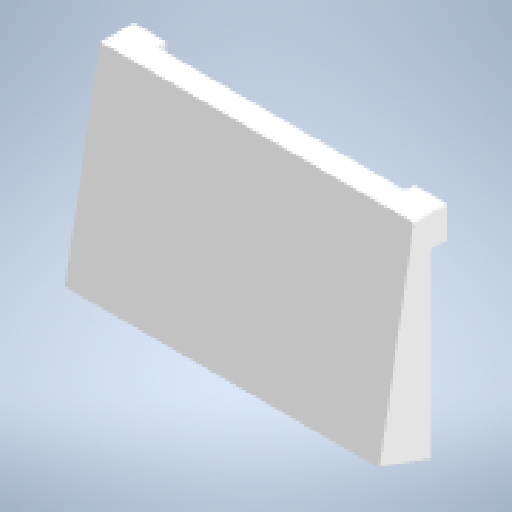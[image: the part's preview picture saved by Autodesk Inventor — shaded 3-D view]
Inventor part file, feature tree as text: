
AUTODESK INVENTOR PART (.ipt)
format: ipt  version: 2024 (Build 280153000, 153)  size: 190,464 bytes
history: native  units: mm
features: extrude x3, sketch x3, projected_geometry x3, fillet x2, plane x1
ambient origin geometry x8: Origin, YZ Plane, XZ Plane, XY Plane, X Axis, Y Axis, Z Axis, Center Point
bodies: Solid1 (feature_tree)
feature tree (12):
  extrude  "Extrusion1"  Depth=20.0mm
  extrude  "Extrusion2"  Depth=20.0mm
  plane  "Work Plane1"
  extrude  "Extrusion4"  Depth=5.0mm TaperAngle=0.0deg
  fillet  "Fillet1"  Radius=5.0mm
  fillet  "Fillet2"  Radius=2.0mm
  sketch  "Sketch1"  dims[d0=20.0mm d1=20.0mm]
  sketch  "Sketch2"  dims[d2=20.0mm d3=20.0mm]
  projected_geometry  "Projected Loop1"
  projected_geometry  "Projected Loop2"
  sketch  "Sketch4"  dims[d4=170.0mm d5=5.0mm d6=0.0mm d7=5.0mm d8=0.0mm d9=-4.25mm d12=2.0mm d13=1.0mm d14=17.453293mm d15=17.453293mm d16=120.0mm d17=20.0mm d18=5.0mm d19=0.0mm]
  projected_geometry  "Projected Loop3"
